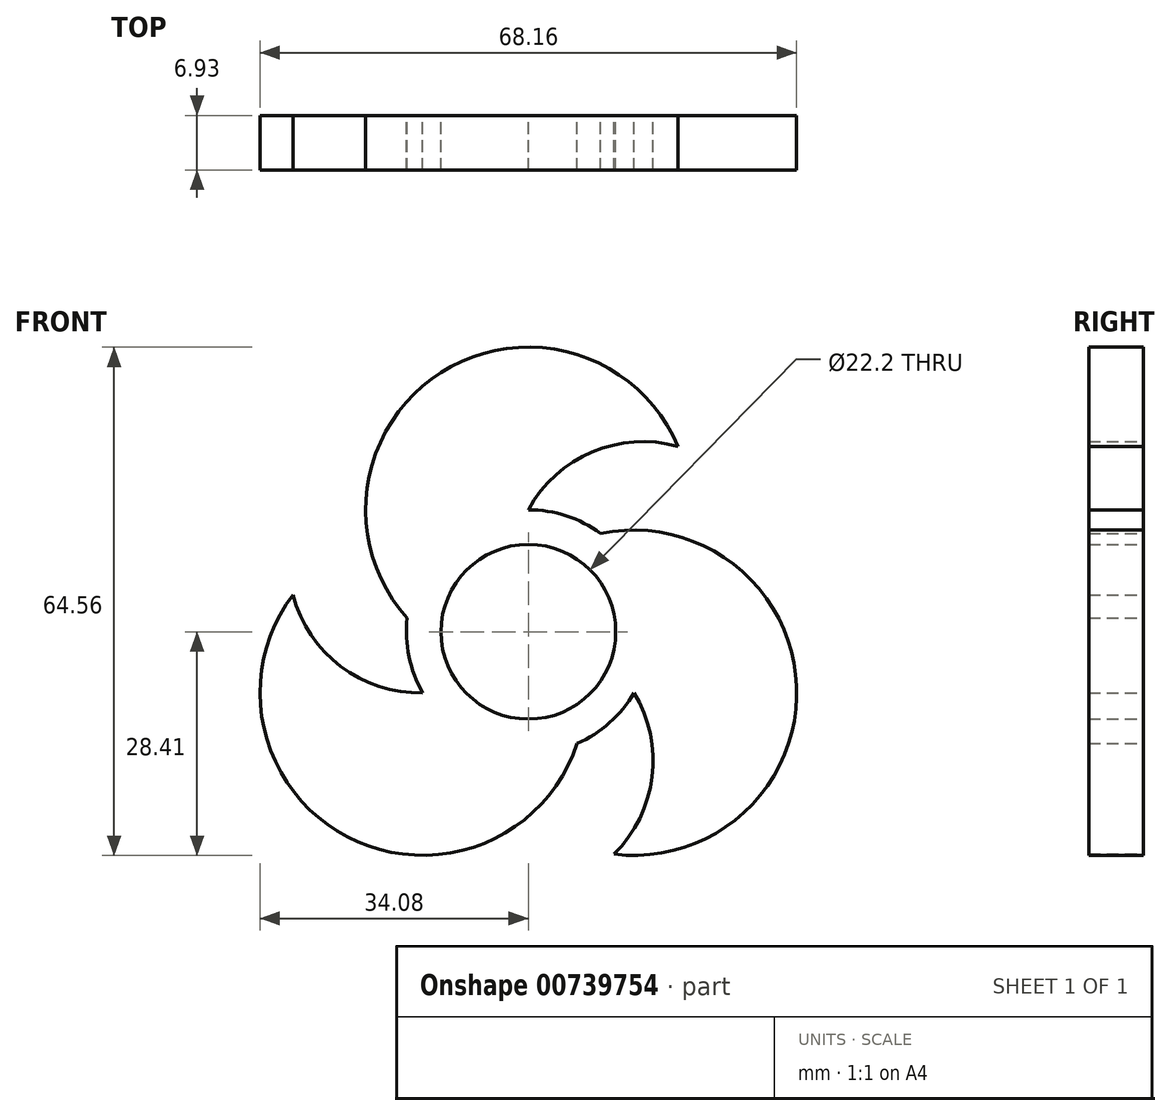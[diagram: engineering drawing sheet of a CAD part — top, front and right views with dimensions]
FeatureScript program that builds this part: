
annotation { "Feature Type Name" : "Feature", "Feature Type Description" : "" }
export const myFeature = defineFeature(function(context is Context, id is Id, definition is map)
    precondition{}
    {
        {
            var Q0;
            Q0=qCreatedBy(makeId("Front.planeOp"),FACE);
            var sketch = newSketch(context, id + "F0", { "sketchPlane" : qUnion([Q0])});
            skCircle(sketch, "E0", {"center": v(0, 0) * mm, "radius": 11.1 * mm});
            skCircle(sketch, "E1", {"center": v(0, 0) * mm, "radius": 15.5 * mm});
            skArc(sketch, "E2", {"start": v(19.02, 23.56) * mm, "mid": v(-11.07, 32.94) * mm, "end": v(-15.4, 1.72) * mm});
            skArc(sketch, "E3", {"start": v(19.02, 23.56) * mm, "mid": v(8.11, 22.83) * mm, "end": v(0, 15.5) * mm});
            skArc(sketch, "E4.1.0", {"start": v(-29.91, 4.7) * mm, "mid": v(-23, -26.05) * mm, "end": v(6.2, -14.2) * mm});
            skArc(sketch, "E4.1.1", {"start": v(-29.91, 4.7) * mm, "mid": v(-23.83, -4.4) * mm, "end": v(-13.42, -7.75) * mm});
            skArc(sketch, "E4.2.0", {"start": v(10.89, -28.25) * mm, "mid": v(34.06, -6.89) * mm, "end": v(9.2, 12.47) * mm});
            skArc(sketch, "E4.2.1", {"start": v(10.89, -28.25) * mm, "mid": v(15.72, -18.44) * mm, "end": v(13.42, -7.75) * mm});
            skLineSegment(sketch, "E5.bottom", {"start": v(34.38, -36.21) * mm, "end": v(-34.38, -36.21) * mm});
            skLineSegment(sketch, "E5.top", {"start": v(34.38, 36.21) * mm, "end": v(-34.38, 36.21) * mm});
            skLineSegment(sketch, "E5.left", {"start": v(34.38, -36.21) * mm, "end": v(34.38, 36.21) * mm});
            skLineSegment(sketch, "E5.right", {"start": v(-34.38, -36.21) * mm, "end": v(-34.38, 36.21) * mm});
            skSolve(sketch);
        }
        {
            var Q0;
            {var subQ0=sQuery(id+"F0.wireOp",EDGE,"E2");Q0=makeQuery(id+"F0.imprint","IMPRINT",FACE,{"disambiguationData":[TD([[makeQuery(id+"F0.imprint","IMPRINT",EDGE,{"derivedFrom":subQ0}),1.0]])]});}
            var Q1;
            {var subQ0=sQuery(id+"F0.wireOp",EDGE,"E4.2.0");Q1=makeQuery(id+"F0.imprint","IMPRINT",FACE,{"disambiguationData":[TD([[makeQuery(id+"F0.imprint","IMPRINT",EDGE,{"derivedFrom":subQ0}),1.0]])]});}
            var Q2;
            Q2=makeQuery(id+"F0.imprint","IMPRINT",FACE,{"disambiguationData":[TD([[makeQuery(id+"F0.imprint","IMPRINT",EDGE,{"derivedFrom":sQuery(id+"F0.wireOp",EDGE,"E0")}),-1.0]])]});
            var Q3;
            {var subQ0=sQuery(id+"F0.wireOp",EDGE,"E4.1.0");Q3=makeQuery(id+"F0.imprint","IMPRINT",FACE,{"disambiguationData":[TD([[makeQuery(id+"F0.imprint","IMPRINT",EDGE,{"derivedFrom":subQ0}),1.0]])]});}
            extrude(context, id + "F1", {"entities" : qUnion([Q0, Q1, Q2, Q3]), "depth" : 6.93 * mm, "offsetDistance" : 25.4 * mm});
        }
    });
